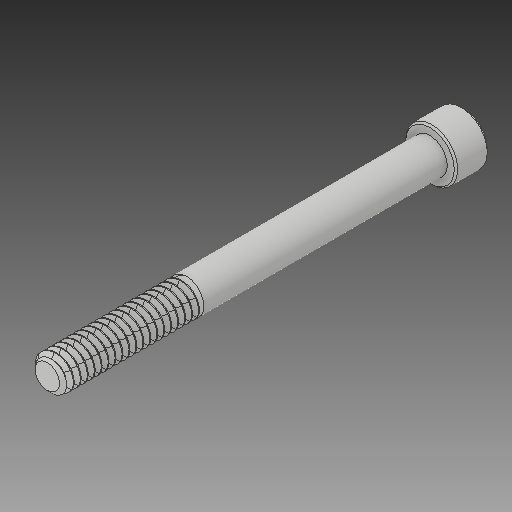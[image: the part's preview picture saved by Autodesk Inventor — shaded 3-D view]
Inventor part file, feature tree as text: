
AUTODESK INVENTOR PART (.ipt)
format: ipt  version: 2017 SP1 (Build 210196100, 196)  size: 532,992 bytes
history: native  units: in
note: dims shown in document units (in); Inventor stores cm internally (conversion verified against a paired STEP export)
features: chamfer x1
ambient origin geometry x8: Origin, YZ Plane, XZ Plane, XY Plane, X Axis, Y Axis, Z Axis, Center Point
bodies: Solid1 (feature_tree)
feature tree (1):
  chamfer  "Chamfer2"  [1 undecoded]
note: 1 required parameter value undecoded (feature->parameter linkage not recoverable at this tier; creation-order binding heuristic only, values carry confidence <= 0.55)
